# Revit family: QF_ELECTROLUXPROFESSIONAL_586819_PUEN12KLEM
name_source: partatom
category: Specialty Equipment
revit_build: Autodesk Revit 2018 (Build: 20190510_1515(x64)
units: mm (PartAtom-declared; Revit-internal decimal feet)

## family parameters
Always vertical = Yes
Cut with Voids When Loaded = No
Part Type = Normal
Room Calculation Point = No
Round Connector Dimension = Use Radius
Shared = Yes
Work Plane-Based = No

## types (2) — shared parameters
50 Hertz Option = No
60 Hertz Option = Yes
Apparent Power = 0 VA
Base Height = 200 mm  [stored 0.656168 ft]
Cold Water Connection Height = 635 mm
Cold Water Size = 1"
Conn Conduit = Yes
Cycle = 60 Hz
Depth = 900 mm  [stored 2.95276 ft]
Direct Waste Size = 0"
Electrical Remarks = 3PH+N 50/60HZ COMPATIBLE
FL Amps = 0 A
HP = 27.6 HP
Height = 900 mm  [stored 2.95276 ft]
Hot Water Connection Height = 715 mm
Hot Water Size = 1"
Indirect Waste Radius Size = 25.4 mm  [stored 0.0833333 ft]
Indirect Waste Size = 2"
Manufacturer = ELECTROLUX
Max Overcurrent Protection = 5 A
Min Ckt Ampacity = 0 A
Phase = 3
URL = www.electrolux.com/foodservice
URL Cutsheet = www.electrolux.com/foodservice
URL Manufacturer = www.electrolux.com/foodservice
Volts = 400 V
Watts = 0 W
Weight = 280 kg
Width = 1400 mm  [stored 4.59318 ft]
zero-valued in all types: Code, Indirect Waste Connection Height

## per-type parameters (varying)
| type | Description | Model |
| 586819_EL. STAT. PRESS. BRAIS. PAN+STEAM+CTS_TAP._125LT (H) | High Productivity Cooking Electric Pressure Braising Pan-125lt Hygienic Profile-with Backsplash CTS & Tap | 586819 |
| 586815_EL. STAT. PRESS. BRAIS. PAN+STEAM_TAP._125LT (H)_C | High Productivity Cooking Electric Pressure Braising Pan-125lt Hygienic Profile-Backsplash & Tap | 586815 |

note: [stored X ft] marks values corroborated as IEEE doubles in the binary element streams (Revit-internal decimal feet)

## geometry (parser evidence)
native form markers: Blend x21, Sweep x2
no freeform markers — native parametric forms only
